# Revit family: LAMP_SETI SOFT 1200
name_source: partatom
category: Modelos genéricos
revit_build: Autodesk Revit 2018 (Build: 20190510_1515(x64)
units: mm (PartAtom-declared; Revit-internal decimal feet)

## family parameters
Anfitrión = Cara
Compartido = No
Corte con vacíos al cargar = No
Cota de conector redondo = Diámetro de uso
Puede alojar armadura = No
Punto de cálculo de habitación = No
Tipo de pieza = Normal

## types (4) — shared parameters
CRI = 80
Dimensions = 120 x 39 x 1200
Elevación por defecto = 1219 mm
Fabricante = LAMP
Gear = Electronic
Initial color = 3000 K
Installation instructions = https://www.lamp.es
Insulation class = II
LED Lifetime = 50.000 L90 B10
Lamp = MID-POWER LED
Last update = 17/02/2022
Luminaire type = Outdoor - Beacon
MacAdam = 3.5
Manufacturer URL = http://www.lamp.es
Manufacturer country = Spain
Manufacturer name = LAMP
Power Supply = 110-240V 50/60Hz
Product URL = https://www.lamp.es
Product datasheet = http://www.lamp.es
Protection rating = IP65 / IK08
Type = MID POWER OSRAM

## per-type parameters (varying)
| type | Descripción | Efficacy | Finish | Initial intensity | Modelo | Photometric web file | Plum | Power | Product code | Weight |
| 88LM 3000 IND ANTHRACITE | SETI SOFT DB 1200 WW ANT. | 8 lm/W | Textured anthracite grey | 106 lm | SE1120D10SO830NAB | Cuerpo seti soft 1200 : 88LM 3000 IND ANTHRACITE | 13 W | 11 W | SE1120D10SO830NAB | 4.61 kg |
| 101LM 3000 DB ANTHRACITE | SETI SOFT DB 1200 WW BK. | 14 lm/W | Texturised black | 185 lm | SE1120D10SO830NBW | Cuerpo seti soft 1200 : 101LM 3000 DB ANTHRACITE | 13 W | 11 W | SE1120D10SO830NBW | 4.61 kg |
| 116LM 3000 IND BLACK | SETI SOFT IND 1200 WW ANT. | 13 lm/W | Textured anthracite grey | 92 lm | SE1120I07SO830NAB | Cuerpo seti soft 1200 : 116LM 3000 IND BLACK | 9 W | 8 W | SE1120I07SO830NAB | 3.74 kg |
| 176LM 3000 DB BLACK | SETI SOFT IND 1200 WW BK. | 11 lm/W | Texturised black | 116 lm | SE1120I07SO830NBW | Cuerpo seti soft 1200 : 176LM 3000 DB BLACK | 9 W | 8 W | SE1120I07SO830NBW | 3.74 kg |
